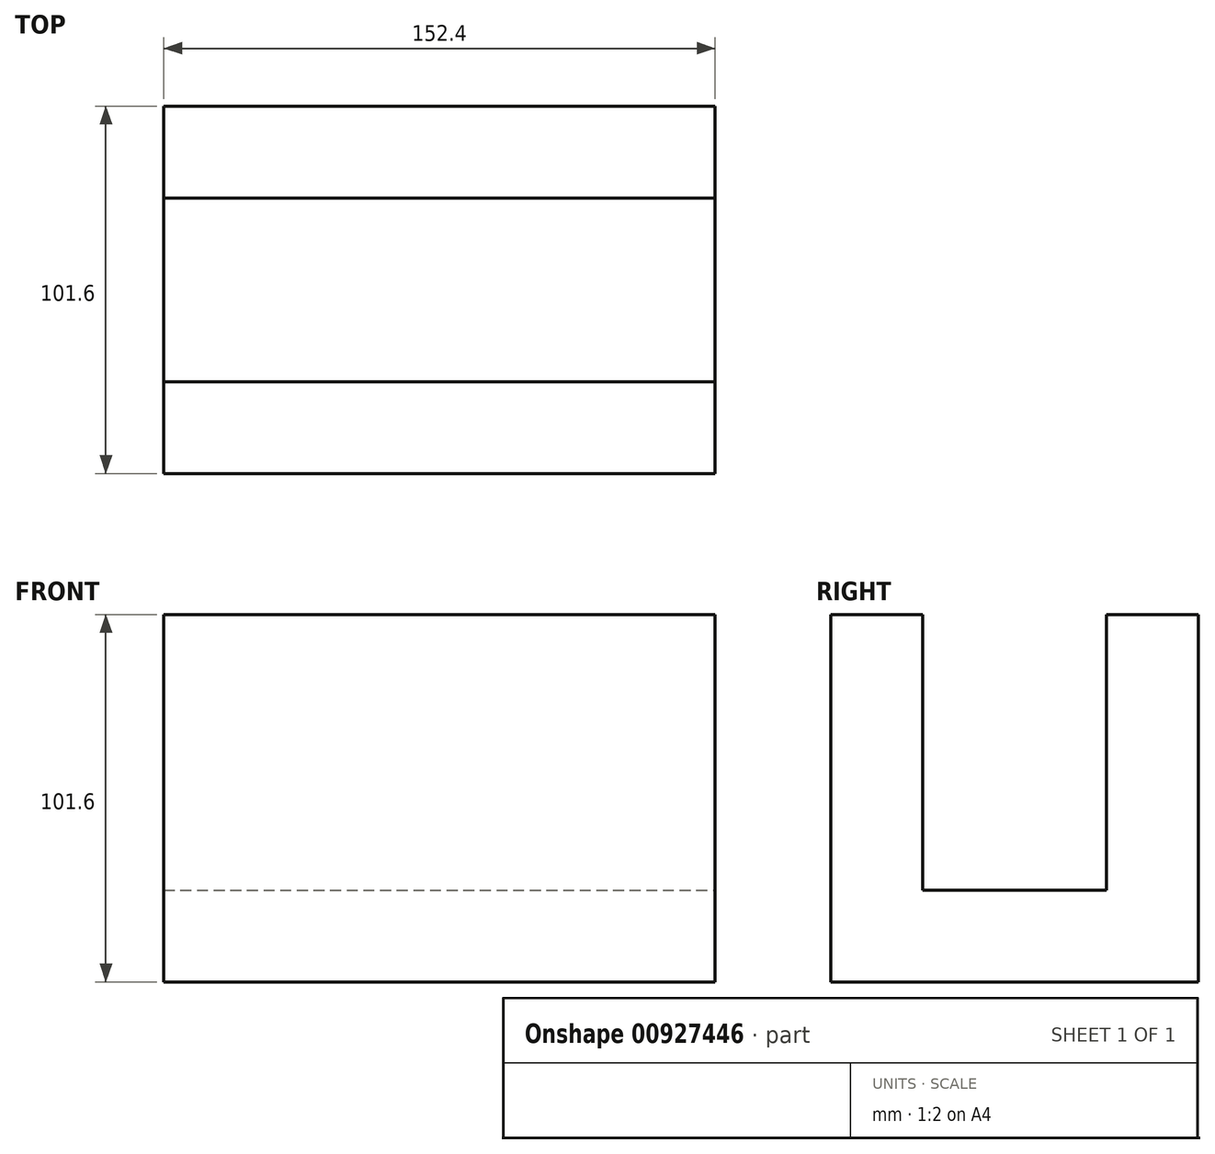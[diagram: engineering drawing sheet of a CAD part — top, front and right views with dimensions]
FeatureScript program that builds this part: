
annotation { "Feature Type Name" : "Feature", "Feature Type Description" : "" }
export const myFeature = defineFeature(function(context is Context, id is Id, definition is map)
    precondition{}
    {
        {
            var Q0;
            Q0=qCreatedBy(makeId("Right.planeOp"),FACE);
            var sketch = newSketch(context, id + "F0", { "sketchPlane" : qUnion([Q0])});
            skLineSegment(sketch, "E0.bottom", {"start": v(0, 0) * mm, "end": v(101.6, 0) * mm});
            skLineSegment(sketch, "E0.top", {"start": v(0, 101.6) * mm, "end": v(101.6, 101.6) * mm});
            skLineSegment(sketch, "E0.left", {"start": v(0, 0) * mm, "end": v(0, 101.6) * mm});
            skLineSegment(sketch, "E0.right", {"start": v(101.6, 0) * mm, "end": v(101.6, 101.6) * mm});
            skSolve(sketch);
        }
        {
            var Q0;
            Q0 = qSketchRegion(id + "F0", true);
            extrude(context, id + "F1", {"entities" : qUnion([Q0]), "oppositeDirection" : true, "depth" : 152.4 * mm, "offsetDistance" : 25.4 * mm});
        }
        {
            var Q0;
            Q0=makeQuery(id+"F1.opExtrude","CAP_FACE",FACE,{"disambiguationData":[OSD([sQuery(id+"F0.wireOp",EDGE,"E0.bottom"),sQuery(id+"F0.wireOp",EDGE,"E0.top"),sQuery(id+"F0.wireOp",EDGE,"E0.left"),sQuery(id+"F0.wireOp",EDGE,"E0.right")])],"isStart":true});
            var sketch = newSketch(context, id + "F2", { "sketchPlane" : qUnion([Q0])});
            skLineSegment(sketch, "E1.bottom", {"start": v(25.4, 101.6) * mm, "end": v(76.2, 101.6) * mm});
            skLineSegment(sketch, "E1.top", {"start": v(25.4, 25.4) * mm, "end": v(76.2, 25.4) * mm});
            skLineSegment(sketch, "E1.left", {"start": v(25.4, 101.6) * mm, "end": v(25.4, 25.4) * mm});
            skLineSegment(sketch, "E1.right", {"start": v(76.2, 101.6) * mm, "end": v(76.2, 25.4) * mm});
            skSolve(sketch);
        }
        {
            var Q0;
            Q0=makeQuery(id+"F2.imprint","IMPRINT",FACE,{"disambiguationData":[TD([[makeQuery(id+"F2.imprint","IMPRINT",EDGE,{"derivedFrom":sQuery(id+"F2.wireOp",EDGE,"E1.bottom")}),-1.0]])]});
            extrude(context, id + "F3", {"entities" : qUnion([Q0]), "operationType" : NewBodyOperationType.REMOVE, "endBound" : BoundingType.THROUGH_ALL, "oppositeDirection" : true, "depth" : 25.4 * mm, "offsetDistance" : 25.4 * mm});
        }
    });
